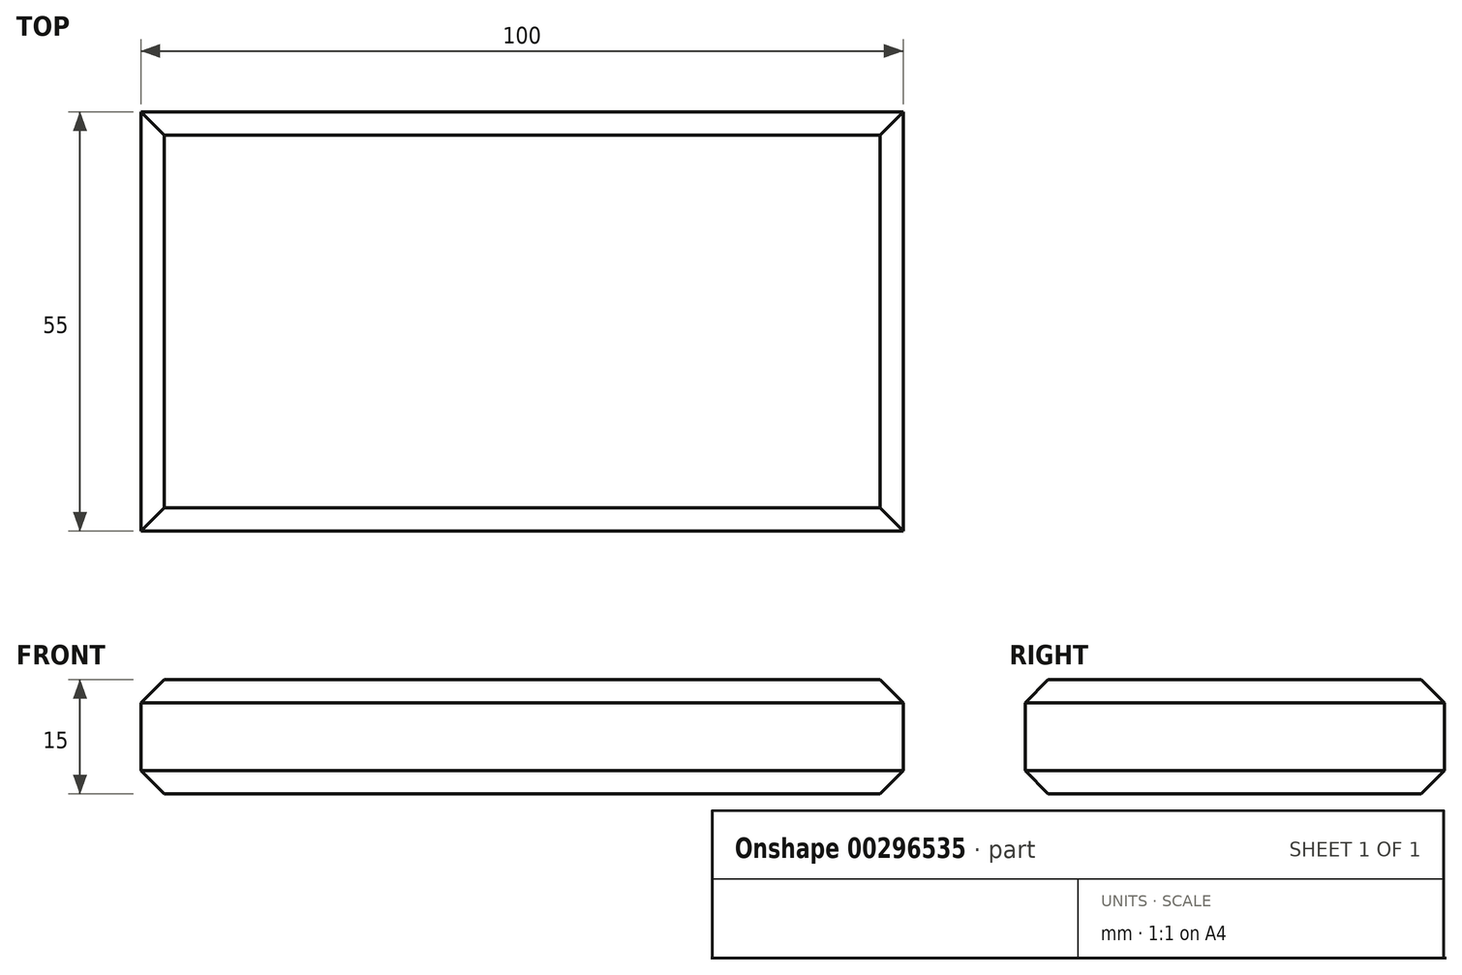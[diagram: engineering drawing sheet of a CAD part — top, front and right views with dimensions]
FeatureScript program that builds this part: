
annotation { "Feature Type Name" : "Feature", "Feature Type Description" : "" }
export const myFeature = defineFeature(function(context is Context, id is Id, definition is map)
    precondition{}
    {
        {
            var Q0;
            Q0=qCreatedBy(makeId("Top.planeOp"),FACE);
            var sketch = newSketch(context, id + "F0", { "sketchPlane" : qUnion([Q0])});
            skLineSegment(sketch, "E0.bottom", {"start": v(50, -27.5) * mm, "end": v(-50, -27.5) * mm});
            skLineSegment(sketch, "E0.top", {"start": v(50, 27.5) * mm, "end": v(-50, 27.5) * mm});
            skLineSegment(sketch, "E0.left", {"start": v(50, -27.5) * mm, "end": v(50, 27.5) * mm});
            skLineSegment(sketch, "E0.right", {"start": v(-50, -27.5) * mm, "end": v(-50, 27.5) * mm});
            skPoint(sketch, "E0.middle", {"position": v(0, 0) * mm});
            skSolve(sketch);
        }
        {
            var Q0;
            Q0=makeQuery(id+"F0.imprint","IMPRINT",FACE,{"disambiguationData":[TD([[makeQuery(id+"F0.imprint","IMPRINT",EDGE,{"derivedFrom":sQuery(id+"F0.wireOp",EDGE,"E0.bottom")}),-1.0]])]});
            extrude(context, id + "F1", {"entities" : qUnion([Q0]), "depth" : 15 * mm});
        }
        {
            var Q0;
            Q0=makeQuery(id+"F1.opExtrude","CAP_EDGE",EDGE,{"disambiguationData":[OSD([sQuery(id+"F0.wireOp",EDGE,"E0.right")])],"isStart":false});
            var Q1;
            Q1=makeQuery(id+"F1.opExtrude","CAP_EDGE",EDGE,{"disambiguationData":[OSD([sQuery(id+"F0.wireOp",EDGE,"E0.top")])],"isStart":false});
            var Q2;
            Q2=makeQuery(id+"F1.opExtrude","CAP_EDGE",EDGE,{"disambiguationData":[OSD([sQuery(id+"F0.wireOp",EDGE,"E0.bottom")])],"isStart":false});
            var Q3;
            Q3=makeQuery(id+"F1.opExtrude","CAP_EDGE",EDGE,{"disambiguationData":[OSD([sQuery(id+"F0.wireOp",EDGE,"E0.left")])],"isStart":false});
            var Q4;
            Q4=makeQuery(id+"F1.opExtrude","CAP_EDGE",EDGE,{"disambiguationData":[OSD([sQuery(id+"F0.wireOp",EDGE,"E0.top")])],"isStart":true});
            var Q5;
            Q5=makeQuery(id+"F1.opExtrude","CAP_EDGE",EDGE,{"disambiguationData":[OSD([sQuery(id+"F0.wireOp",EDGE,"E0.right")])],"isStart":true});
            var Q6;
            Q6=makeQuery(id+"F1.opExtrude","CAP_EDGE",EDGE,{"disambiguationData":[OSD([sQuery(id+"F0.wireOp",EDGE,"E0.bottom")])],"isStart":true});
            var Q7;
            Q7=makeQuery(id+"F1.opExtrude","CAP_EDGE",EDGE,{"disambiguationData":[OSD([sQuery(id+"F0.wireOp",EDGE,"E0.left")])],"isStart":true});
            chamfer(context, id + "F2", {"entities" : qUnion([Q0, Q1, Q2, Q3, Q4, Q5, Q6, Q7]), "width" : 3.05 * mm, "tangentPropagation" : true});
        }
    });
